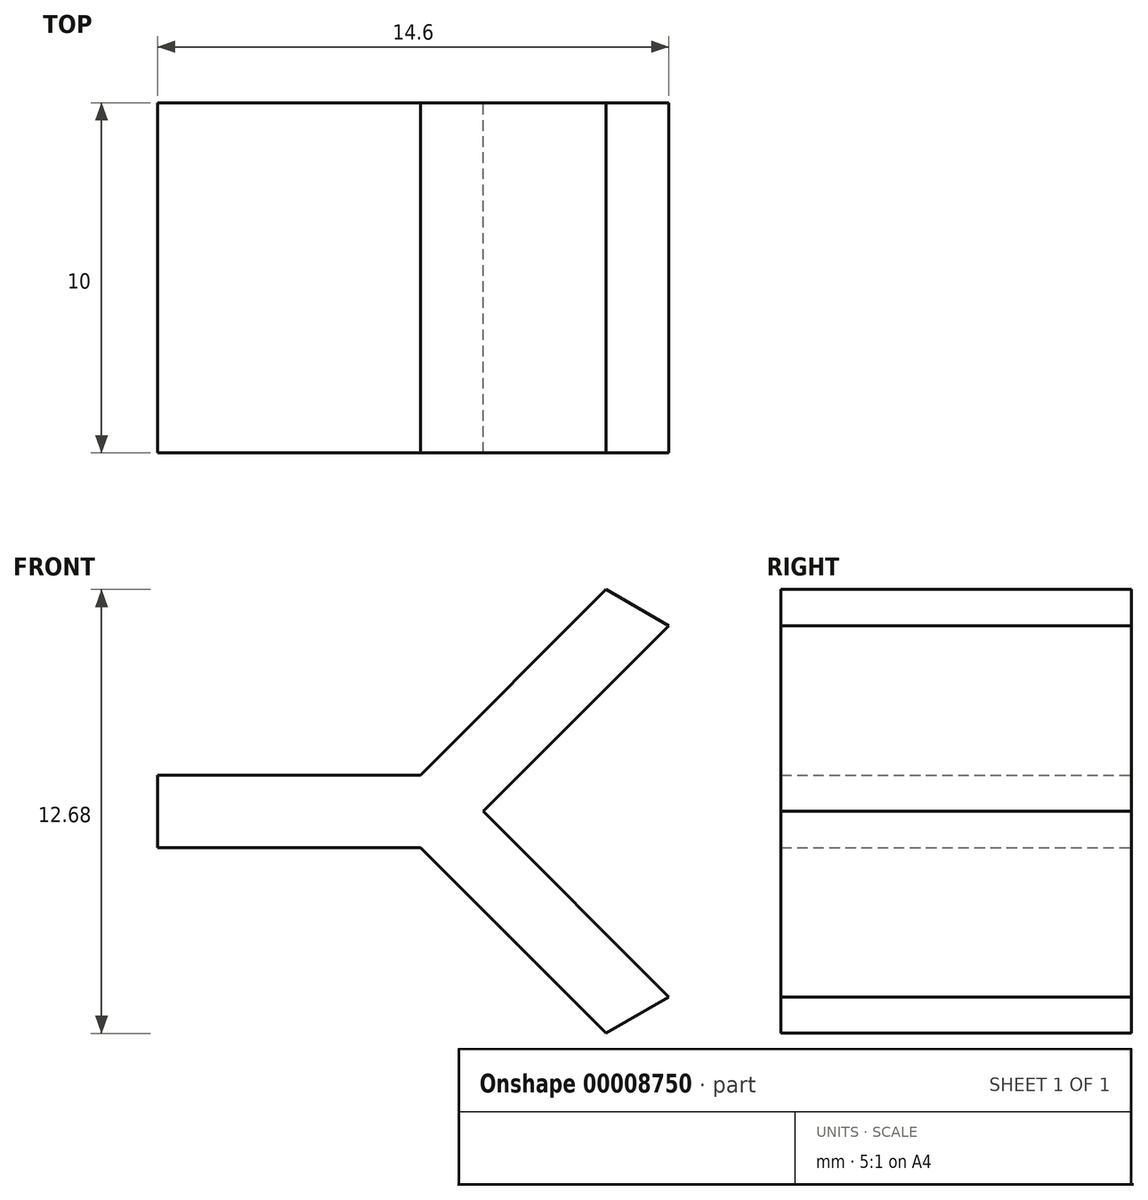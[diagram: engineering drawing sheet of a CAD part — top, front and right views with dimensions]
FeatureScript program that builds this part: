
annotation { "Feature Type Name" : "Feature", "Feature Type Description" : "" }
export const myFeature = defineFeature(function(context is Context, id is Id, definition is map)
    precondition{}
    {
        {
            var Q0;
            Q0=qCreatedBy(makeId("Front.planeOp"),FACE);
            var sketch = newSketch(context, id + "F0", { "sketchPlane" : qUnion([Q0])});
            skLineSegment(sketch, "E0", {"start": v(-7.88, 79.76) * mm, "end": v(-0.38, 79.76) * mm});
            skLineSegment(sketch, "E1", {"start": v(-0.38, 79.76) * mm, "end": v(4.93, 85.06) * mm});
            skLineSegment(sketch, "E2", {"start": v(6.72, 84.03) * mm, "end": v(1.42, 78.72) * mm});
            skLineSegment(sketch, "E3", {"start": v(1.42, 78.72) * mm, "end": v(6.72, 73.42) * mm});
            skLineSegment(sketch, "E4", {"start": v(4.93, 72.38) * mm, "end": v(-0.38, 77.69) * mm});
            skLineSegment(sketch, "E5", {"start": v(-0.38, 77.69) * mm, "end": v(-7.88, 77.69) * mm});
            skLineSegment(sketch, "E6", {"start": v(22.41, 78.72) * mm, "end": v(-25.53, 78.72) * mm, "construction": true});
            skLineSegment(sketch, "E7", {"start": v(-0.38, 79.76) * mm, "end": v(1.42, 78.72) * mm, "construction": true});
            skLineSegment(sketch, "E8", {"start": v(1.42, 78.72) * mm, "end": v(-0.38, 77.69) * mm, "construction": true});
            skLineSegment(sketch, "E9", {"start": v(-0.38, 79.76) * mm, "end": v(-0.38, 77.69) * mm, "construction": true});
            skLineSegment(sketch, "E10", {"start": v(6.72, 84.03) * mm, "end": v(4.93, 85.06) * mm, "construction": true});
            skLineSegment(sketch, "E11", {"start": v(6.72, 73.42) * mm, "end": v(4.93, 72.38) * mm, "construction": true});
            skLineSegment(sketch, "E12", {"start": v(-7.88, 79.76) * mm, "end": v(-7.88, 77.69) * mm});
            skLineSegment(sketch, "E13", {"start": v(4.93, 85.06) * mm, "end": v(6.72, 84.03) * mm});
            skLineSegment(sketch, "E14", {"start": v(6.72, 73.42) * mm, "end": v(4.93, 72.38) * mm});
            skSolve(sketch);
        }
        {
            var Q0;
            Q0 = qSketchRegion(id + "F0", true);
            extrude(context, id + "F1", {"entities" : qUnion([Q0]), "depth" : 10 * mm});
        }
    });
